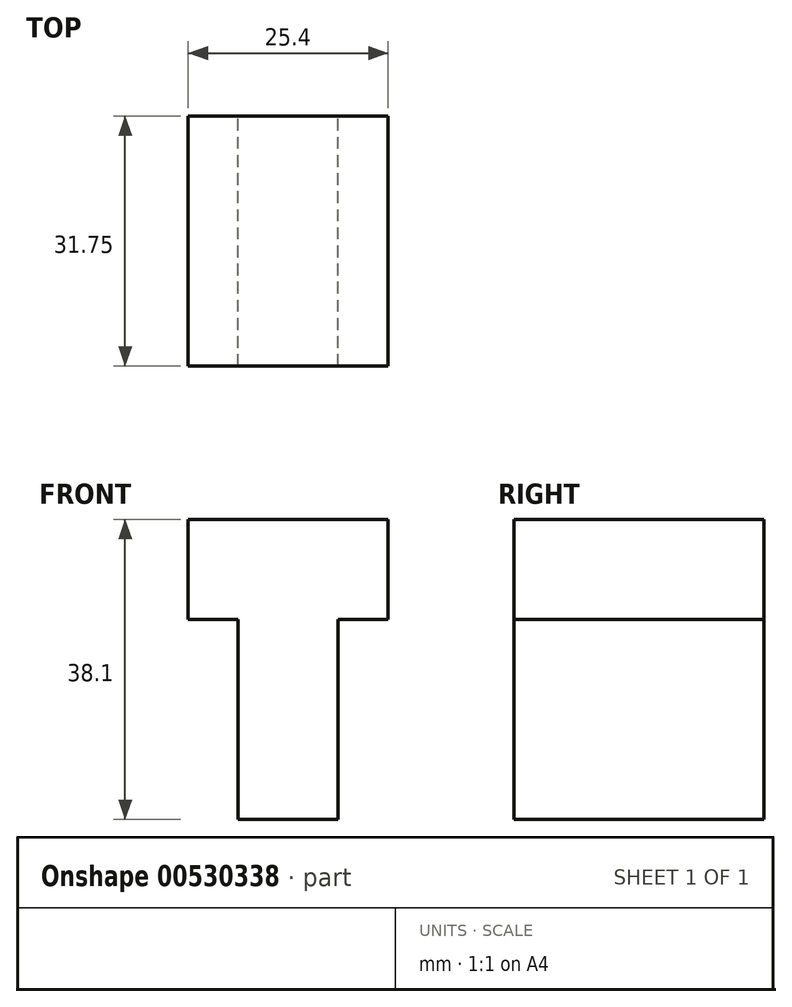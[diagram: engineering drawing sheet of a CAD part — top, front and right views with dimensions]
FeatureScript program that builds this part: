
annotation { "Feature Type Name" : "Feature", "Feature Type Description" : "" }
export const myFeature = defineFeature(function(context is Context, id is Id, definition is map)
    precondition{}
    {
        {
            var Q0;
            Q0=qCreatedBy(makeId("Front.planeOp"),FACE);
            var sketch = newSketch(context, id + "F0", { "sketchPlane" : qUnion([Q0])});
            skLineSegment(sketch, "E0", {"start": v(-44.82, 25.4) * mm, "end": v(-44.82, 0) * mm});
            skLineSegment(sketch, "E1", {"start": v(-44.82, 0) * mm, "end": v(-32.12, 0) * mm});
            skLineSegment(sketch, "E2", {"start": v(-32.12, 0) * mm, "end": v(-32.12, 25.4) * mm});
            skLineSegment(sketch, "E3", {"start": v(-44.82, 25.4) * mm, "end": v(-51.17, 25.4) * mm});
            skLineSegment(sketch, "E4", {"start": v(-32.12, 25.4) * mm, "end": v(-25.77, 25.4) * mm});
            skLineSegment(sketch, "E5", {"start": v(-51.17, 25.4) * mm, "end": v(-51.17, 38.1) * mm});
            skLineSegment(sketch, "E6", {"start": v(-25.77, 25.4) * mm, "end": v(-25.77, 38.1) * mm});
            skLineSegment(sketch, "E7", {"start": v(-51.17, 38.1) * mm, "end": v(-25.77, 38.1) * mm});
            skSolve(sketch);
        }
        {
            var Q0;
            Q0 = qSketchRegion(id + "F0", true);
            extrude(context, id + "F1", {"entities" : qUnion([Q0]), "depth" : 31.75 * mm, "offsetDistance" : 25.4 * mm});
        }
    });
